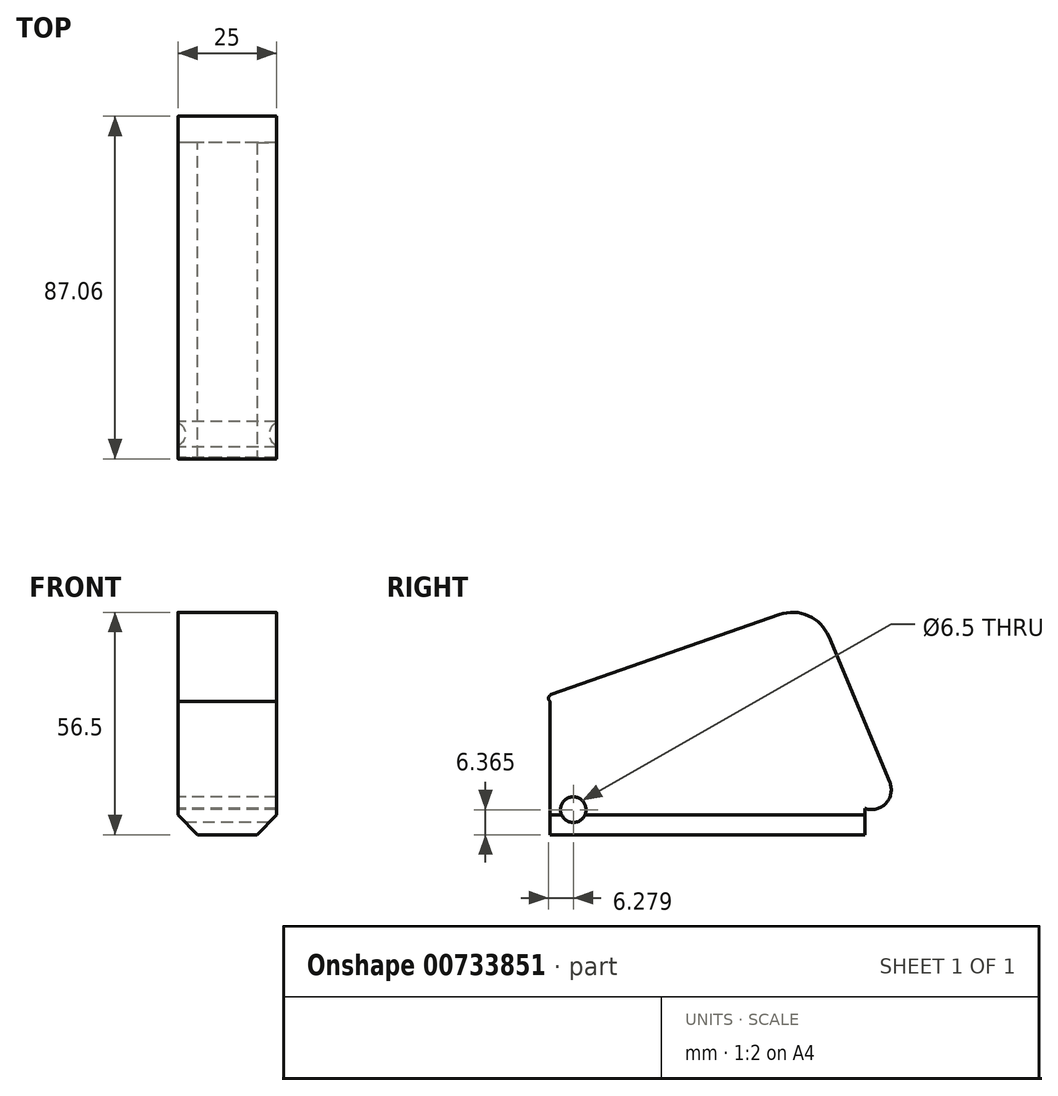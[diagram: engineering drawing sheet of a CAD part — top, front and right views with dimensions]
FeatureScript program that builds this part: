
annotation { "Feature Type Name" : "Feature", "Feature Type Description" : "" }
export const myFeature = defineFeature(function(context is Context, id is Id, definition is map)
    precondition{}
    {
        {
            var Q0;
            Q0=qCreatedBy(makeId("Right.planeOp"),FACE);
            var sketch = newSketch(context, id + "F0", { "sketchPlane" : qUnion([Q0])});
            skLineSegment(sketch, "E0.bottom", {"start": v(35.15, 0) * mm, "end": v(-44.85, 0) * mm});
            skLineSegment(sketch, "E0.top", {"start": v(35.15, 35) * mm, "end": v(-44.85, 35) * mm});
            skLineSegment(sketch, "E0.left", {"start": v(35.15, 0) * mm, "end": v(35.15, 35) * mm});
            skLineSegment(sketch, "E0.right", {"start": v(-44.85, 0) * mm, "end": v(-44.85, 35) * mm});
            skLineSegment(sketch, "E1", {"start": v(-44.85, 35) * mm, "end": v(35.15, 27.38) * mm});
            skSolve(sketch);
        }
        {
            var Q0;
            {var subQ0=sQuery(id+"F0.wireOp",EDGE,"E0.bottom");Q0=makeQuery(id+"F0.imprint","IMPRINT",FACE,{"disambiguationData":[TD([[makeQuery(id+"F0.imprint","IMPRINT",EDGE,{"derivedFrom":subQ0}),-1.0]])]});}
            extrude(context, id + "F1", {"entities" : qUnion([Q0]), "depth" : 25 * mm, "offsetDistance" : 25 * mm});
        }
        {
            var Q0;
            Q0=qCreatedBy(makeId("Right.planeOp"),FACE);
            var sketch = newSketch(context, id + "F2", { "sketchPlane" : qUnion([Q0])});
            skLineSegment(sketch, "E2", {"start": v(45.74, 3.1) * mm, "end": v(22.35, 59.06) * mm});
            skLineSegment(sketch, "E3", {"start": v(22.35, 59.06) * mm, "end": v(-50.18, 33.6) * mm});
            skLineSegment(sketch, "E4", {"start": v(-47.18, 34.66) * mm, "end": v(45.74, 3.1) * mm});
            skSolve(sketch);
        }
        {
            var Q0;
            {var subQ0=sQuery(id+"F2.wireOp",EDGE,"E2");Q0=makeQuery(id+"F2.imprint","IMPRINT",FACE,{"disambiguationData":[TD([[makeQuery(id+"F2.imprint","IMPRINT",EDGE,{"derivedFrom":subQ0}),1.0]])]});}
            extrude(context, id + "F3", {"entities" : qUnion([Q0]), "operationType" : NewBodyOperationType.ADD, "depth" : 25 * mm, "offsetDistance" : 25 * mm});
        }
        {
            var Q0;
            Q0=makeQuery(id+"F3.boolean.opBoolean","MERGE",FACE,{"derivedFrom":[makeQuery(id+"F1.opExtrude","CAP_FACE",FACE,{"disambiguationData":[OSD([sQuery(id+"F0.wireOp",EDGE,"E0.bottom"),sQuery(id+"F0.wireOp",EDGE,"E0.left"),sQuery(id+"F0.wireOp",EDGE,"E0.right"),sQuery(id+"F0.wireOp",EDGE,"E1")])],"isStart":true}),makeQuery(id+"F3.opExtrude","CAP_FACE",FACE,{"disambiguationData":[OSD([sQuery(id+"F2.wireOp",EDGE,"E2"),sQuery(id+"F2.wireOp",EDGE,"E3"),sQuery(id+"F2.wireOp",EDGE,"E4")])],"isStart":true})]});
            var sketch = newSketch(context, id + "F4", { "sketchPlane" : qUnion([Q0])});
            skCircle(sketch, "E5", {"center": v(38.93, 6.37) * mm, "radius": 3.25 * mm});
            skSolve(sketch);
        }
        {
            var Q0;
            Q0=sQuery(id+"F4.wireOp",VERTEX,"E5.center");
            var Q1;
            Q1=makeQuery(id+"F1.opExtrude","SWEPT_BODY",BODY,{"disambiguationData":[OSD([sQuery(id+"F0.wireOp",EDGE,"E0.bottom"),sQuery(id+"F0.wireOp",EDGE,"E0.left"),sQuery(id+"F0.wireOp",EDGE,"E0.right"),sQuery(id+"F0.wireOp",EDGE,"E1")])]});
            hole(context, id + "F5", {"style" : HoleStyle.SIMPLE, "endStyle" : HoleEndStyle.THROUGH, "holeDiameter" : 6.5 * mm, "majorDiameter" : 5 * mm, "isTappedThrough" : true, "tappedDepth" : 12 * mm, "tapClearance" : 3, "locations" : qUnion([Q0]), "scope" : qUnion([Q1])});
        }
        {
            var Q0;
            Q0=makeQuery(id+"F3.opExtrude","SWEPT_EDGE",EDGE,{"disambiguationData":[OSD([sQuery(id+"F2.wireOp",EDGE,"E2"),sQuery(id+"F2.wireOp",EDGE,"E3")])]});
            fillet(context, id + "F6", {"entities" : qUnion([Q0]), "radius" : 10 * mm, "tangentPropagation" : true, "allowEdgeOverflow" : false});
        }
        {
            var Q0;
            Q0=makeQuery(id+"F3.opExtrude","SWEPT_EDGE",EDGE,{"disambiguationData":[OSD([sQuery(id+"F2.wireOp",EDGE,"E2"),sQuery(id+"F2.wireOp",EDGE,"E4")])]});
            fillet(context, id + "F7", {"entities" : qUnion([Q0]), "radius" : 5 * mm, "tangentPropagation" : true, "allowEdgeOverflow" : false});
        }
        {
            var Q0;
            Q0=makeQuery(id+"F3.opExtrude","SWEPT_EDGE",EDGE,{"disambiguationData":[OSD([sQuery(id+"F2.wireOp",EDGE,"E3"),sQuery(id+"F2.wireOp",EDGE,"E4")])]});
            fillet(context, id + "F8", {"entities" : qUnion([Q0]), "radius" : 1 * mm, "tangentPropagation" : true, "allowEdgeOverflow" : false});
        }
        {
            var Q0;
            Q0=makeQuery(id+"F1.opExtrude","CAP_EDGE",EDGE,{"disambiguationData":[OSD([sQuery(id+"F0.wireOp",EDGE,"E0.bottom")])],"isStart":false});
            chamfer(context, id + "F9", {"entities" : qUnion([Q0]), "width" : 5 * mm, "tangentPropagation" : true});
        }
        {
            var Q0;
            Q0=makeQuery(id+"F1.opExtrude","CAP_EDGE",EDGE,{"disambiguationData":[OSD([sQuery(id+"F0.wireOp",EDGE,"E0.bottom")])],"isStart":true});
            chamfer(context, id + "F10", {"entities" : qUnion([Q0]), "width" : 5 * mm, "tangentPropagation" : true});
        }
    });
